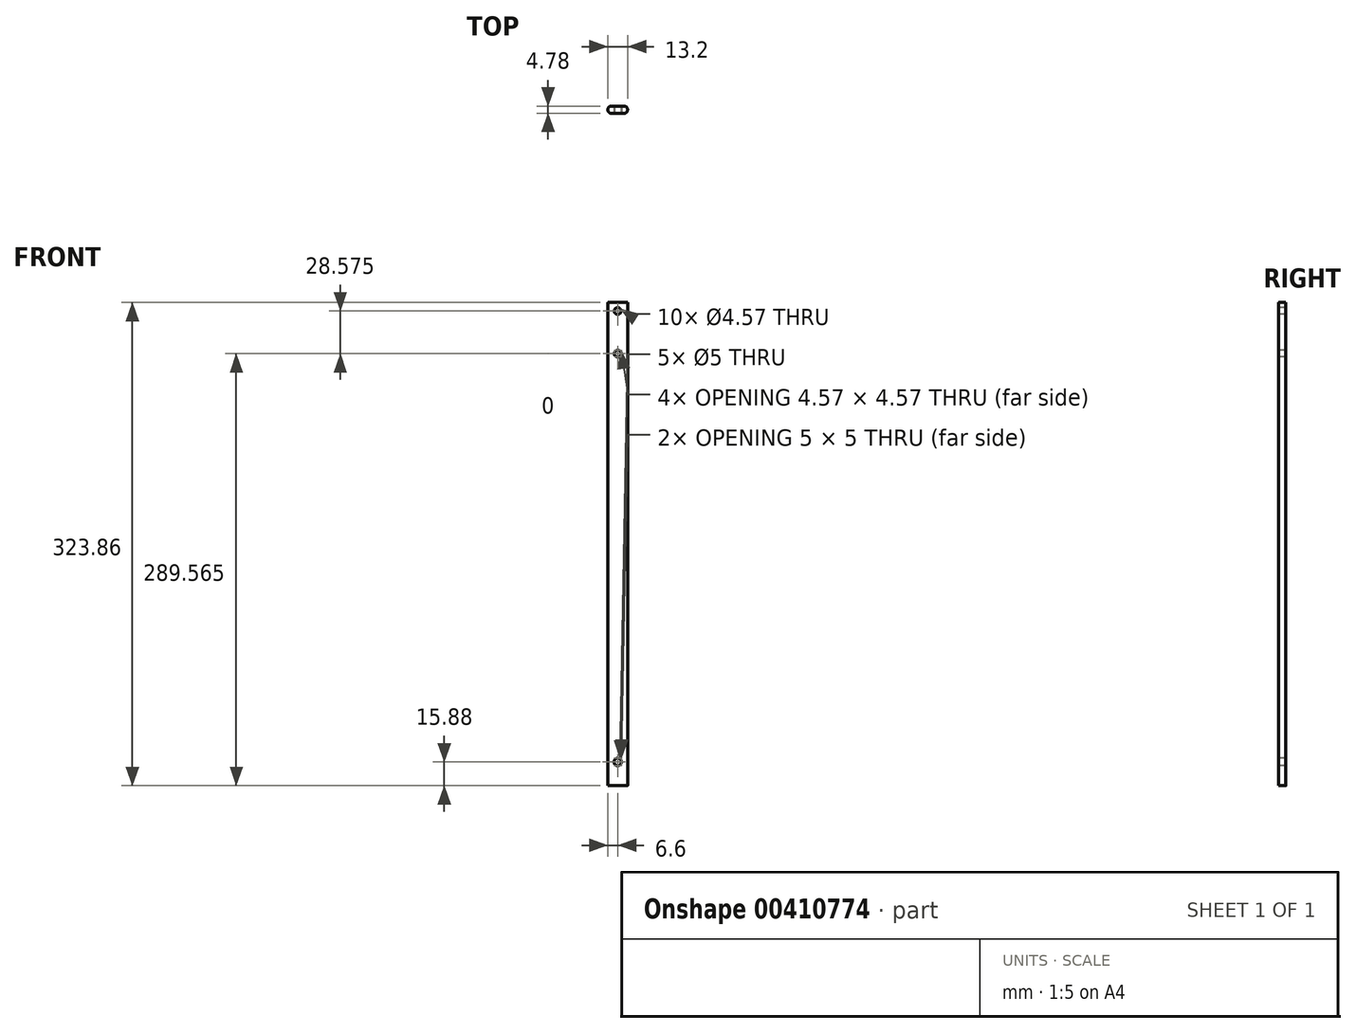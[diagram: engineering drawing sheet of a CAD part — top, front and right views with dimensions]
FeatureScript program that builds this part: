
annotation { "Feature Type Name" : "Feature", "Feature Type Description" : "" }
export const myFeature = defineFeature(function(context is Context, id is Id, definition is map)
    precondition{}
    {
        {
            var Q0;
            Q0=qCreatedBy(makeId("Top.planeOp"),FACE);
            var sketch = newSketch(context, id + "F0", { "sketchPlane" : qUnion([Q0])});
            skLineSegment(sketch, "E0.bottom", {"start": v(-4.32, 2.39) * mm, "end": v(4.32, 2.39) * mm});
            skLineSegment(sketch, "E0.top", {"start": v(-4.32, -2.39) * mm, "end": v(4.32, -2.39) * mm});
            skLineSegment(sketch, "E0.left", {"start": v(-6.6, 0.1) * mm, "end": v(-6.6, -0.1) * mm});
            skLineSegment(sketch, "E0.right", {"start": v(6.6, 0.1) * mm, "end": v(6.6, -0.1) * mm});
            skPoint(sketch, "E0.middle", {"position": v(0, 0) * mm});
            skPoint(sketch, "E1.visualSharp", {"position": v(-6.6, 2.39) * mm});
            skArc(sketch, "E1.filletArc", {"start": v(-4.32, 2.39) * mm, "mid": v(-5.93, 1.72) * mm, "end": v(-6.6, 0.1) * mm});
            skPoint(sketch, "E2.visualSharp", {"position": v(-6.6, -2.39) * mm});
            skArc(sketch, "E2.filletArc", {"start": v(-6.6, -0.1) * mm, "mid": v(-5.93, -1.72) * mm, "end": v(-4.32, -2.39) * mm});
            skPoint(sketch, "E3.visualSharp", {"position": v(6.6, 2.39) * mm});
            skArc(sketch, "E3.filletArc", {"start": v(6.6, 0.1) * mm, "mid": v(5.93, 1.72) * mm, "end": v(4.32, 2.39) * mm});
            skPoint(sketch, "E4.visualSharp", {"position": v(6.6, -2.39) * mm});
            skArc(sketch, "E4.filletArc", {"start": v(4.32, -2.39) * mm, "mid": v(5.93, -1.72) * mm, "end": v(6.6, -0.1) * mm});
            skSolve(sketch);
        }
        {
            var Q0;
            Q0=makeQuery(id+"F0.imprint","IMPRINT",FACE,{"disambiguationData":[TD([[makeQuery(id+"F0.imprint","IMPRINT",EDGE,{"derivedFrom":sQuery(id+"F0.wireOp",EDGE,"E0.bottom")}),-1.0]])]});
            extrude(context, id + "F1", {"entities" : qUnion([Q0]), "depth" : 323.85 * mm, "offsetDistance" : 25.4 * mm, "symmetric" : true});
        }
        {
            var Q0;
            Q0=makeQuery(id+"F1.opExtrude","SWEPT_FACE",FACE,{"disambiguationData":[OSD([sQuery(id+"F0.wireOp",EDGE,"E0.top")])]});
            var sketch = newSketch(context, id + "F2", { "sketchPlane" : qUnion([Q0])});
            skCircle(sketch, "E5", {"center": v(0, 156.21) * mm, "radius": 2.29 * mm});
            skCircle(sketch, "E6", {"center": v(0, 127.64) * mm, "radius": 2.29 * mm});
            skSolve(sketch);
        }
        {
            var Q0;
            Q0=makeQuery(id+"F2.imprint","IMPRINT",FACE,{"disambiguationData":[TD([[makeQuery(id+"F2.imprint","IMPRINT",EDGE,{"derivedFrom":sQuery(id+"F2.wireOp",EDGE,"E5")}),1.0]])]});
            var Q1;
            Q1=makeQuery(id+"F2.imprint","IMPRINT",FACE,{"disambiguationData":[TD([[makeQuery(id+"F2.imprint","IMPRINT",EDGE,{"derivedFrom":sQuery(id+"F2.wireOp",EDGE,"E6")}),1.0]])]});
            extrude(context, id + "F3", {"entities" : qUnion([Q0, Q1]), "operationType" : NewBodyOperationType.REMOVE, "oppositeDirection" : true, "depth" : 25.4 * mm, "offsetDistance" : 25.4 * mm});
        }
        {
            var Q0;
            Q0=makeQuery(id+"F1.opExtrude","SWEPT_FACE",FACE,{"disambiguationData":[OSD([sQuery(id+"F0.wireOp",EDGE,"E0.top")])]});
            var sketch = newSketch(context, id + "F4", { "sketchPlane" : qUnion([Q0])});
            skCircle(sketch, "E7", {"center": v(0, -146.05) * mm, "radius": 2.5 * mm});
            skSolve(sketch);
        }
        {
            var Q0;
            Q0=makeQuery(id+"F4.imprint","IMPRINT",FACE,{"disambiguationData":[TD([[makeQuery(id+"F4.imprint","IMPRINT",EDGE,{"derivedFrom":sQuery(id+"F4.wireOp",EDGE,"E7")}),1.0]])]});
            extrude(context, id + "F5", {"entities" : qUnion([Q0]), "operationType" : NewBodyOperationType.REMOVE, "oppositeDirection" : true, "depth" : 25.4 * mm, "offsetDistance" : 25.4 * mm});
        }
    });
